# Revit family: IS_ConnectAir_A7029_BIM_IT
name_source: partatom
category: Plumbing Fixtures
revit_build: Autodesk Revit 2017 (Build: 20160225_1515(x64)
units: mm (PartAtom-declared; Revit-internal decimal feet)

## family parameters
Always vertical = No
Cut with Voids When Loaded = No
OmniClass Number = 23.45.55.17
OmniClass Title = Mixing Faucets
Part Type = Normal
Room Calculation Point = No
Round Connector Dimension = Use Diameter
Shared = No
Work Plane-Based = No

## types (1)
- A7029AA - C.AIR MISC LAVABO INC CROMO KIT 2 - 185
    Accessori = http://www.idealstandard.it
    AltezzaNominale = 106 mm  [stored 0.347769 ft]
    Autore = Ideal Standard
    BIMobject main category = Sanitary
    BIMobject main category code = sanitary
    BOSUseNativeGeometries = 1
    Brand url = http://www.idealstandard.co.uk
    Caratteristiche = C.AIR MISC LAVABO INC CROMO KIT 2 - 185
    CodiceABarre = 4015413342100
    CodiceDiPrestazione = EN
    Colore = cromo
    Connessione = piombatura
    Cost = 0 $
    CostoDiSostituzione = 0 $
    Date of publishing = 2018_04_19
    Description = C.AIR MISC LAVABO INC CROMO KIT 2 - 185
    DescrizioneClassifcazioneUni2015 = IfcSanitaryTerminalType
    Dimensione = 193 x 201 x 106 mm
    EAN code = https://4015413342100
    Edition number = 1
    Finitura = cromo
    Forma = scolpito
    Garanzia = garanzia del produttore
    IFC Classification = Sanitary Terminal
    IfcEsportaCome = IfcSanitaryTerminalType
    InformazioniDiProdotto = http://www.idealstandard.it
    Installation instructions = http://www.idealstandard.it
    InstruzioniInstallazione = http://www.idealstandard.it
    LarghezzaNominale = 193 mm  [stored 0.633202 ft]
    LunghezzaNominale = 201 mm  [stored 0.659449 ft]
    Manufacturer name = Ideal Standard
    Material main = Brassware
    Materiale = brassware
    Model = A7029AA
    ModelloDiRiferimento = C.AIR MISC LAVABO INC CROMO KIT 2 - 185
    NBS Reference Code = 45-35-70/
    NBS Reference Description = Wash Basin And Trough Water Supply Fittings
    Nome = ISI_IdealStandard_BasinMixers_ConnectAir_A7029AA
    NomeOggettoBim = ISI_IdealStandard_BasinMixers_ConnectAir_A7029AA
    Nominal height = 106
    Nominal width = 193
    NominalHeight = 106 mm  [stored 0.347769 ft]
    NominalLength = 201 mm  [stored 0.659449 ft]
    NominalWidth = 193 mm  [stored 0.633202 ft]
    NumeroDiModello = A7029AA
    OmniClass Code = 23-31 11 00
    OmniClass Description = Faucets
    PartiDiRicambio = http://www.idealstandard.it
    PesoNetto = 1.57 Kg
    Product Guid = 83168f9d-92f9-4fa5-a1f8-bffbc8e4ff85
    Product SKU = A7029
    Product certification = http://www.idealstandard.it
    Product data url = https://bimobject.com
    Product family = Sanitary
    Product group = BASIN MIXER
    Product name = C.AIR MISC LAVABO INC CROMO KIT 2 - 185
    Product url = http://www.idealstandard.it
    ProfonditàNominale = 201 mm  [stored 0.659449 ft]
    QR code = http://bimobject.com
    Revisione = 1
    Riferimento = Pr_40_20_87_98
    RiferimentoClassificazioneUni2015 = Washbasin taps
    Size = 193 x 201 x 106 mm
    Sostenibilità = riciclabile
    Spazio = interno
    Technical description = http://www.idealstandard.it
    Telefono = 800 652 290
    TipoDiDato = Fisso
    TipoEspotazioneIfc = BASIN MIXER
    TipologiaVaso = Altro
    URL = http://www.idealstandard.it
    Uniclass 2.0 Code = Pr_40_20_87_98
    Uniclass 2.0 Description = Washbasin taps
    Uniclass 2015 Code = Pr_40_20_87_98
    Uniclass 2015 Name = Washbasin taps
    UnitàDurata = anno
    UnitàDurataGaranzia = anno
    UnitàLineare = millimetro
    UnitàMonetaria = €
    UnitàSuperficie = millimetro
    UnitàVolume = litro
    Versione = 1
    VersioneClassificazioneUni2015 = Products v1.1
    Weight Net (Kg) = 1.57

note: [stored X ft] marks values corroborated as IEEE doubles in the binary element streams (Revit-internal decimal feet)

## geometry (parser evidence)
native form markers: Sweep x2
no freeform markers — native parametric forms only
